# Revit family: AKTMDLED
name_source: partatom
category: Lighting Fixtures
revit_build: Autodesk Revit 2014 (Build: 20130308_1515(x64)
units: mm (PartAtom-declared; Revit-internal decimal feet)

## types (2) — shared parameters
Apparent Load = 24 VA
Application = Meeting Room, Commons Areas, Classrooms and Offices, Halls/Dorms, Lobby, Conference Room
Assembly Code = D5020210
Default Elevation = 48.000"
Description = The AKTM Series of line voltage LED track heads provide powerful, high quality light for commercial and retail applications with long life and significant energy savings.
Features = High Output - 900 up to 2500 delivered lumens
Available in 2700K, 3000K, or 3500K
80 or 90 CRI
2-Step MacAdam Ellipse Color Consistency
Factory configurable beam spread options - 18° to 55°
High performance driver compatible with forward and reverse phases dimming controls
Equipped with integral heat sink providing a minimum of 50,000 hrs at 80% lumen maintenance
Luminaires are certified by a National Recognized Testing Lab (NTRL), either UL or CSA
5-year warranty
Lamp = LED
Lens = Hubbell-Glass
Load Classification = Lighting
Manufacturer = Prescolite
Model = AKTMDLED
Power Factor = 1
Product Documentation Link = https://hubbellcdn.com
Product Page URL = https://www.hubbell.com
Tilt Angle = 120.00°
Total Input Wattage = 24 W
URL = https://www.hubbell.com
Voltage = 120 V
Wattage Comments = 24 W
zz Angle1 = 120.00°

## per-type parameters (varying)
| type | Fixture Color |
| AKTMDLED-BL | Hubbell-Paint-Black |
| AKTMDLED-WH | Hubbell-Paint-White |

## geometry (parser evidence)
native form markers: Sweep x7
no freeform markers — native parametric forms only
